# Revit family: in-wall_bottle_filling_station_wall_mounting_frame-elkay-LZWSGRNM8K 1
name_source: partatom
category: Plumbing Fixtures
units: mm (PartAtom-declared; Revit-internal decimal feet)

## family parameters
Cut with Voids When Loaded = No
Host = Face
Maintain Annotation Orientation = No
OmniClass Number = 23.65.70.14.11
OmniClass Title = Drinking Fountains/Coolers
Part Type = Normal
Room Calculation Point = No
Round Connector Dimension = Use Diameter
Shared = No

## types (1)
- LZWSGRNM8K (Bottle Filling Station with Mounting Frame Filtered Refrigerated Stainless )
    Activation Method = Electronic Bottle Filler Sensor
    Approx. Shipping Weight (lbs) = 81
    Assembly Code = D2010800
    CW Connection = No
    Chilling Capacity = 8
    Current = 0 A
    Cut Height = 40 "
    Cutting Width thickness = 4.5 "
    Default Elevation = 48 "
    Description = ezH2O®  In-Wall Bottle Filling Station with Mounting Frame High Efficiency Filtered Refrigerated Stainless
    Dimensions (L x W x H) = 19 3/4 inch x 3 1/2 inch x 40 13/16 inch
    HW Connection = No
    Height = 40.813 "
    Inlet connection = 0.38 "
    Installation Location = Indoor
    Length = 19.75 "
    Main Material = Finish-Elkay-Stainless Steel
    Manufacturer = Elkay Manufacturer Company
    Manufacturer Brand = Elkay (by Zurn Elkay Water Solutions)
    Model = LZWSGRNM8K
    Mounting Type = Wall Mount (Inwall Frame/Plate)
    Number of Poles = 1
    Outlet connection = 1.25 "
    Power Factor = 0
    Product Documentation Link = https://www.elkayfiles.com
    Product Installation Sheet URL = https://www.elkayfiles.com
    Product Page URL = https://www.elkay.com
    Product Weight (lbs) = 66
    Product data URL = https://www.bimobject.com
    Repair Parts URL = https://www.elkayfiles.com
    Second material = Elkay-Transparent
    Supply Line = 17.947 "
    URL = https://www.elkay.com
    Vent Connection = No
    Voltage = 115 V
    Waste Connection = No
    Waste Line = 25.875 "
    Width = 3.5 "
    Width of Cut = 18.75 "
    basin radius = 3.9 "
    thickness = 0.63 "

## geometry (parser evidence)
native form markers: Sweep x6
no freeform markers — native parametric forms only
